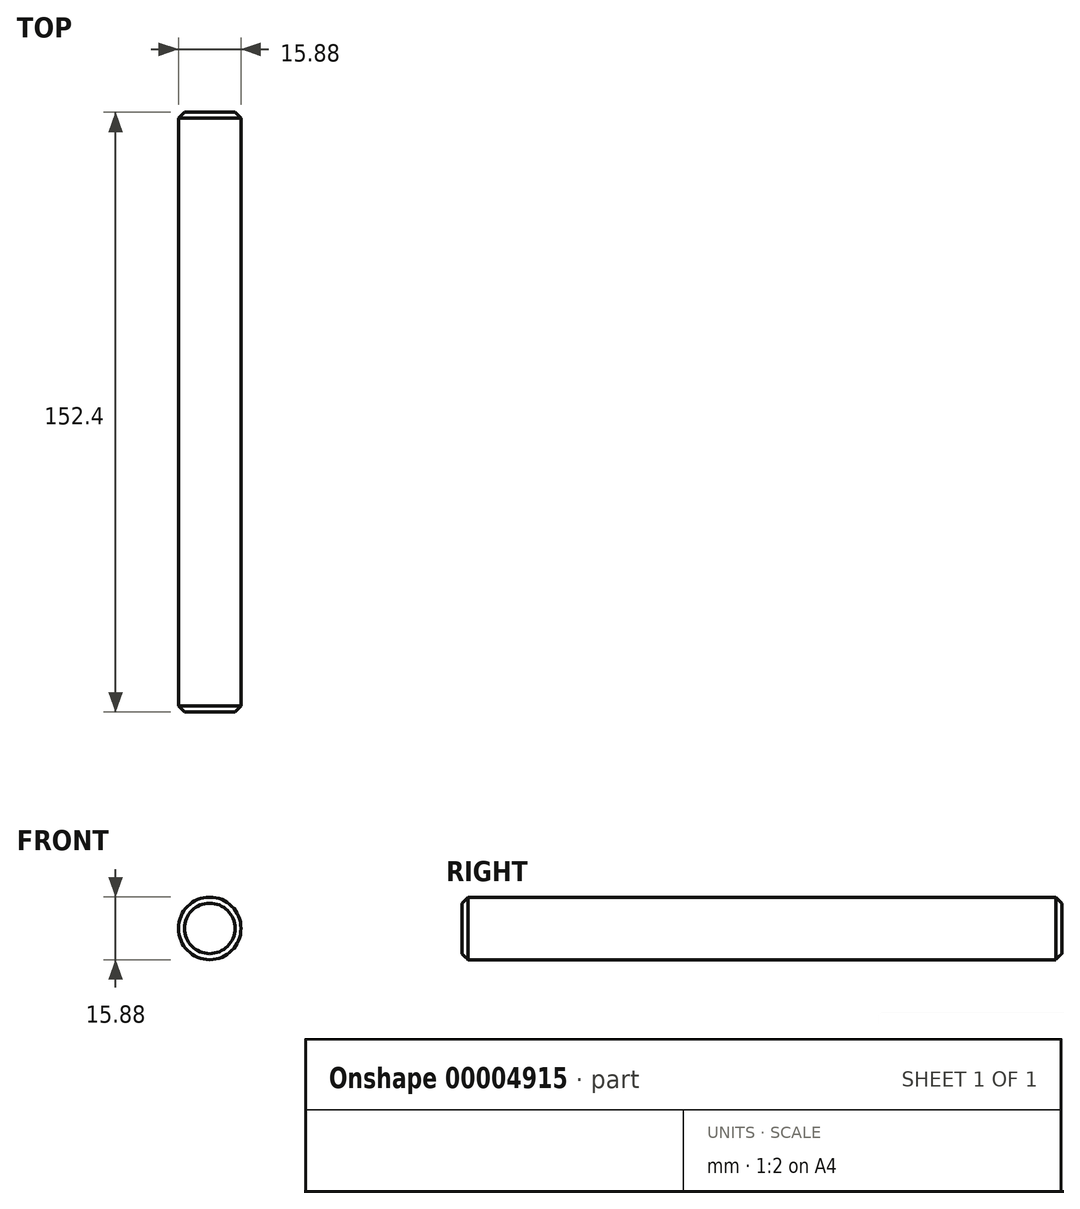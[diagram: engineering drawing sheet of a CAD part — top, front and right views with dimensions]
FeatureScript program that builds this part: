
annotation { "Feature Type Name" : "Feature", "Feature Type Description" : "" }
export const myFeature = defineFeature(function(context is Context, id is Id, definition is map)
    precondition{}
    {
        {
            var Q0;
            Q0=qCreatedBy(makeId("Front.planeOp"),FACE);
            var sketch = newSketch(context, id + "F0", { "sketchPlane" : qUnion([Q0])});
            skCircle(sketch, "E0", {"center": v(0, 0) * mm, "radius": 7.94 * mm});
            skSolve(sketch);
        }
        {
            var Q0;
            Q0=makeQuery(id+"F0.imprint","IMPRINT",FACE,{"disambiguationData":[TD([[makeQuery(id+"F0.imprint","IMPRINT",EDGE,{"derivedFrom":sQuery(id+"F0.wireOp",EDGE,"E0")}),1.0]])]});
            extrude(context, id + "F1", {"entities" : qUnion([Q0]), "endBound" : BoundingType.SYMMETRIC, "depth" : 152.4 * mm});
        }
        {
            var Q0;
            Q0=makeQuery(id+"F1.opExtrude","CAP_EDGE",EDGE,{"disambiguationData":[OSD([sQuery(id+"F0.wireOp",EDGE,"E0")])],"isStart":false});
            var Q1;
            Q1=makeQuery(id+"F1.opExtrude","CAP_EDGE",EDGE,{"disambiguationData":[OSD([sQuery(id+"F0.wireOp",EDGE,"E0")])],"isStart":true});
            chamfer(context, id + "F2", {"entities" : qUnion([Q0, Q1]), "width" : 1.52 * mm, "tangentPropagation" : true});
        }
    });
